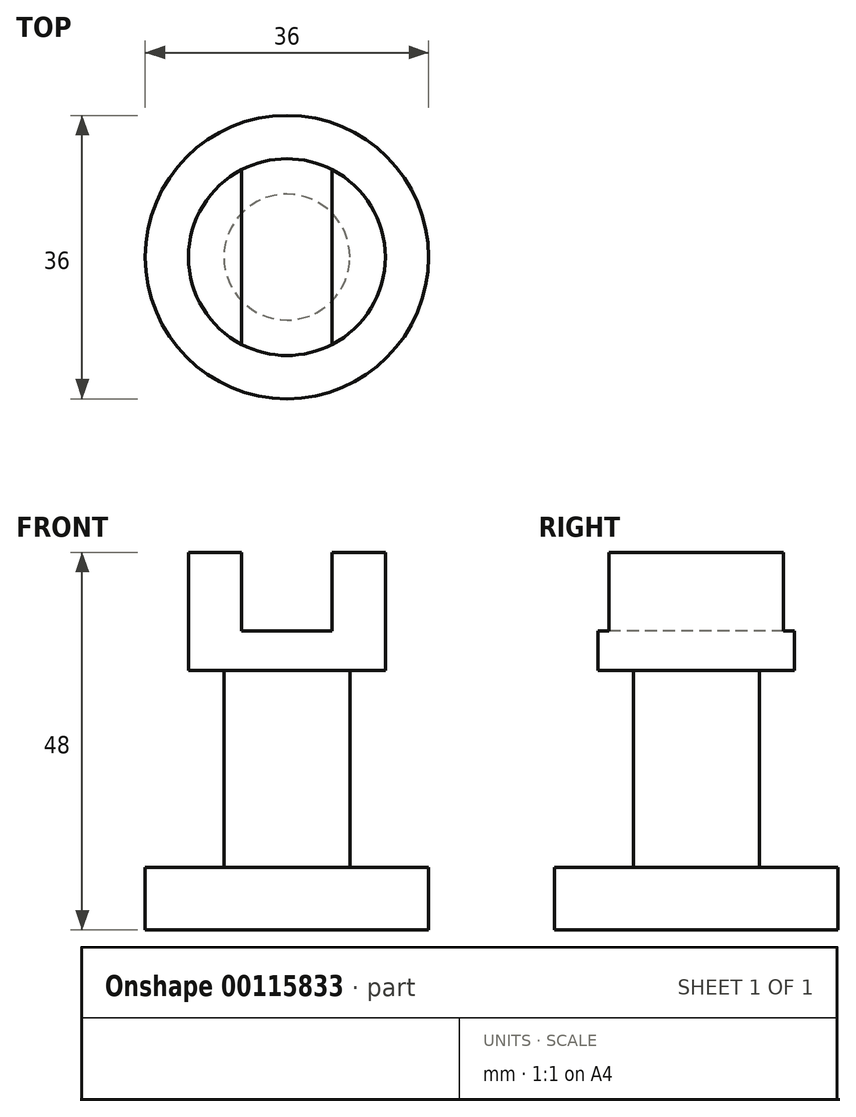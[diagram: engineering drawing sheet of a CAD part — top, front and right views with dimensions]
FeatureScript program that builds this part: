
annotation { "Feature Type Name" : "Feature", "Feature Type Description" : "" }
export const myFeature = defineFeature(function(context is Context, id is Id, definition is map)
    precondition{}
    {
        {
            var Q0;
            Q0=qCreatedBy(makeId("Front.planeOp"),FACE);
            var sketch = newSketch(context, id + "F0", { "sketchPlane" : qUnion([Q0])});
            skLineSegment(sketch, "E0.bottom", {"start": v(-8, 0) * mm, "end": v(0, 0) * mm});
            skLineSegment(sketch, "E0.top", {"start": v(-8, -25) * mm, "end": v(0, -25) * mm});
            skLineSegment(sketch, "E0.left", {"start": v(-8, 0) * mm, "end": v(-8, -25) * mm});
            skLineSegment(sketch, "E1.bottom", {"start": v(-18, -25) * mm, "end": v(0, -25) * mm});
            skLineSegment(sketch, "E1.top", {"start": v(-18, -33) * mm, "end": v(0, -33) * mm});
            skLineSegment(sketch, "E1.left", {"start": v(-18, -25) * mm, "end": v(-18, -33) * mm});
            skLineSegment(sketch, "E2.bottom", {"start": v(-12.5, 15) * mm, "end": v(0, 15) * mm});
            skLineSegment(sketch, "E2.top", {"start": v(-12.5, 0) * mm, "end": v(0, 0) * mm});
            skLineSegment(sketch, "E2.left", {"start": v(-12.5, 15) * mm, "end": v(-12.5, 0) * mm});
            skPoint(sketch, "E3", {"position": v(0, 15) * mm});
            skPoint(sketch, "E4", {"position": v(0, -33) * mm});
            skPoint(sketch, "E5", {"position": v(0, -25) * mm});
            skLineSegment(sketch, "E6", {"start": v(0, 38.72) * mm, "end": v(0, -61.28) * mm, "construction": true});
            skLineSegment(sketch, "E7", {"start": v(0, 15) * mm, "end": v(0, 0) * mm});
            skLineSegment(sketch, "E8", {"start": v(0, 0) * mm, "end": v(0, -33) * mm});
            skSolve(sketch);
        }
        {
            var Q0;
            Q0 = qSketchRegion(id + "F0", true);
            var Q1;
            Q1=sQuery(id+"F0.wireOp",EDGE,"E6");
            revolve(context, id + "F1", {"entities" : qUnion([Q0]), "axis" : qUnion([Q1]), "revolveType" : RevolveType.FULL});
        }
        {
            var Q0;
            Q0=makeQuery(id+"F1.opRevolve","SWEPT_FACE",FACE,{"disambiguationData":[OSD([sQuery(id+"F0.wireOp",EDGE,"E2.bottom")])]});
            var sketch = newSketch(context, id + "F2", { "sketchPlane" : qUnion([Q0])});
            skLineSegment(sketch, "E9", {"start": v(-5.75, 11.1) * mm, "end": v(-5.75, -11.1) * mm});
            skLineSegment(sketch, "E10", {"start": v(5.75, 11.1) * mm, "end": v(5.75, -11.1) * mm});
            skArc(sketch, "E11", {"start": v(-5.75, 11.1) * mm, "mid": v(0, 12.5) * mm, "end": v(5.75, 11.1) * mm});
            skArc(sketch, "E12", {"start": v(5.75, -11.1) * mm, "mid": v(0, -12.5) * mm, "end": v(-5.75, -11.1) * mm});
            skSolve(sketch);
        }
        {
            var Q0;
            Q0=makeQuery(id+"F2.imprint","IMPRINT",FACE,{"disambiguationData":[TD([[makeQuery(id+"F2.imprint","IMPRINT",EDGE,{"derivedFrom":sQuery(id+"F2.wireOp",EDGE,"E9")}),1.0]])]});
            extrude(context, id + "F3", {"entities" : qUnion([Q0]), "operationType" : NewBodyOperationType.REMOVE, "oppositeDirection" : true, "depth" : 10 * mm});
        }
    });
